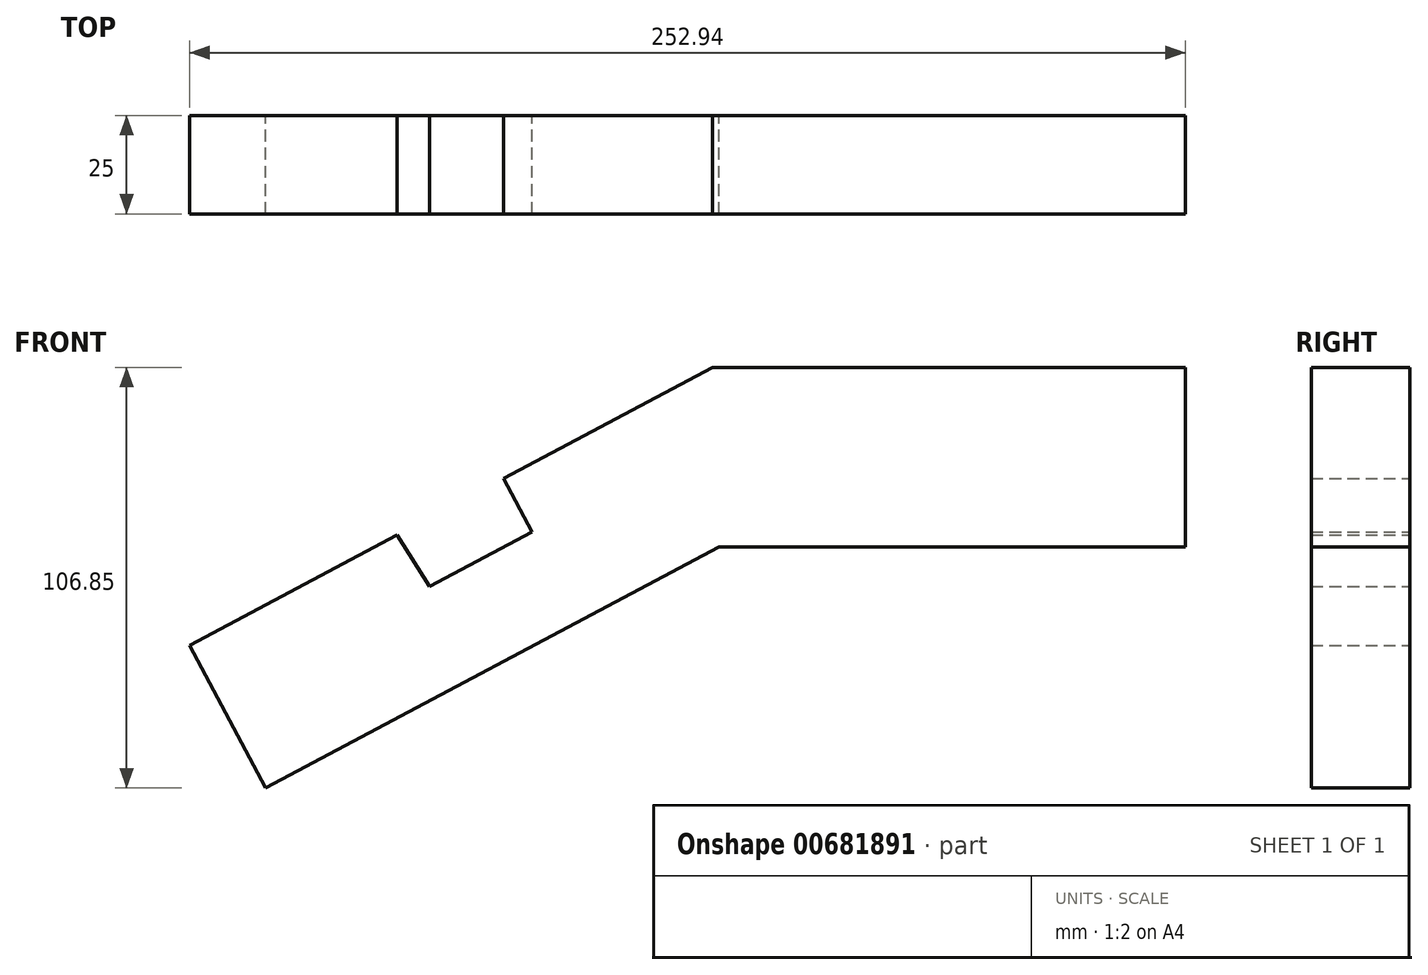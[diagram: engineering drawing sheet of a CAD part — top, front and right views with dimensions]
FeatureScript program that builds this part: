
annotation { "Feature Type Name" : "Feature", "Feature Type Description" : "" }
export const myFeature = defineFeature(function(context is Context, id is Id, definition is map)
    precondition{}
    {
        {
            var Q0;
            Q0=qCreatedBy(makeId("Front.planeOp"),FACE);
            var sketch = newSketch(context, id + "F0", { "sketchPlane" : qUnion([Q0])});
            skLineSegment(sketch, "E0", {"start": v(0, 0) * mm, "end": v(120.1, 0) * mm});
            skLineSegment(sketch, "E1", {"start": v(0, 0) * mm, "end": v(-53.1, -28.25) * mm});
            skLineSegment(sketch, "E2", {"start": v(120.1, 0) * mm, "end": v(120.1, -45.56) * mm});
            skLineSegment(sketch, "E3", {"start": v(120.1, -45.56) * mm, "end": v(0, -45.56) * mm});
            skLineSegment(sketch, "E4.0", {"start": v(1.64, -45.56) * mm, "end": v(-113.57, -106.85) * mm});
            skLineSegment(sketch, "E5", {"start": v(-132.83, -70.65) * mm, "end": v(-113.57, -106.85) * mm});
            skLineSegment(sketch, "E6", {"start": v(-132.83, -70.65) * mm, "end": v(-80.1, -42.6) * mm});
            skLineSegment(sketch, "E7", {"start": v(-53.1, -28.25) * mm, "end": v(-45.87, -41.86) * mm});
            skLineSegment(sketch, "E8", {"start": v(-45.87, -41.86) * mm, "end": v(-71.87, -55.7) * mm});
            skLineSegment(sketch, "E9", {"start": v(-71.87, -55.7) * mm, "end": v(-80.1, -42.6) * mm});
            skLineSegment(sketch, "E10.trimOffspring", {"start": v(-80.1, -42.6) * mm, "end": v(-132.83, -70.65) * mm});
            skSolve(sketch);
        }
        {
            var Q0;
            Q0 = qSketchRegion(id + "F0", true);
            extrude(context, id + "F1", {"entities" : qUnion([Q0]), "depth" : 25 * mm, "offsetDistance" : 25 * mm});
        }
    });
